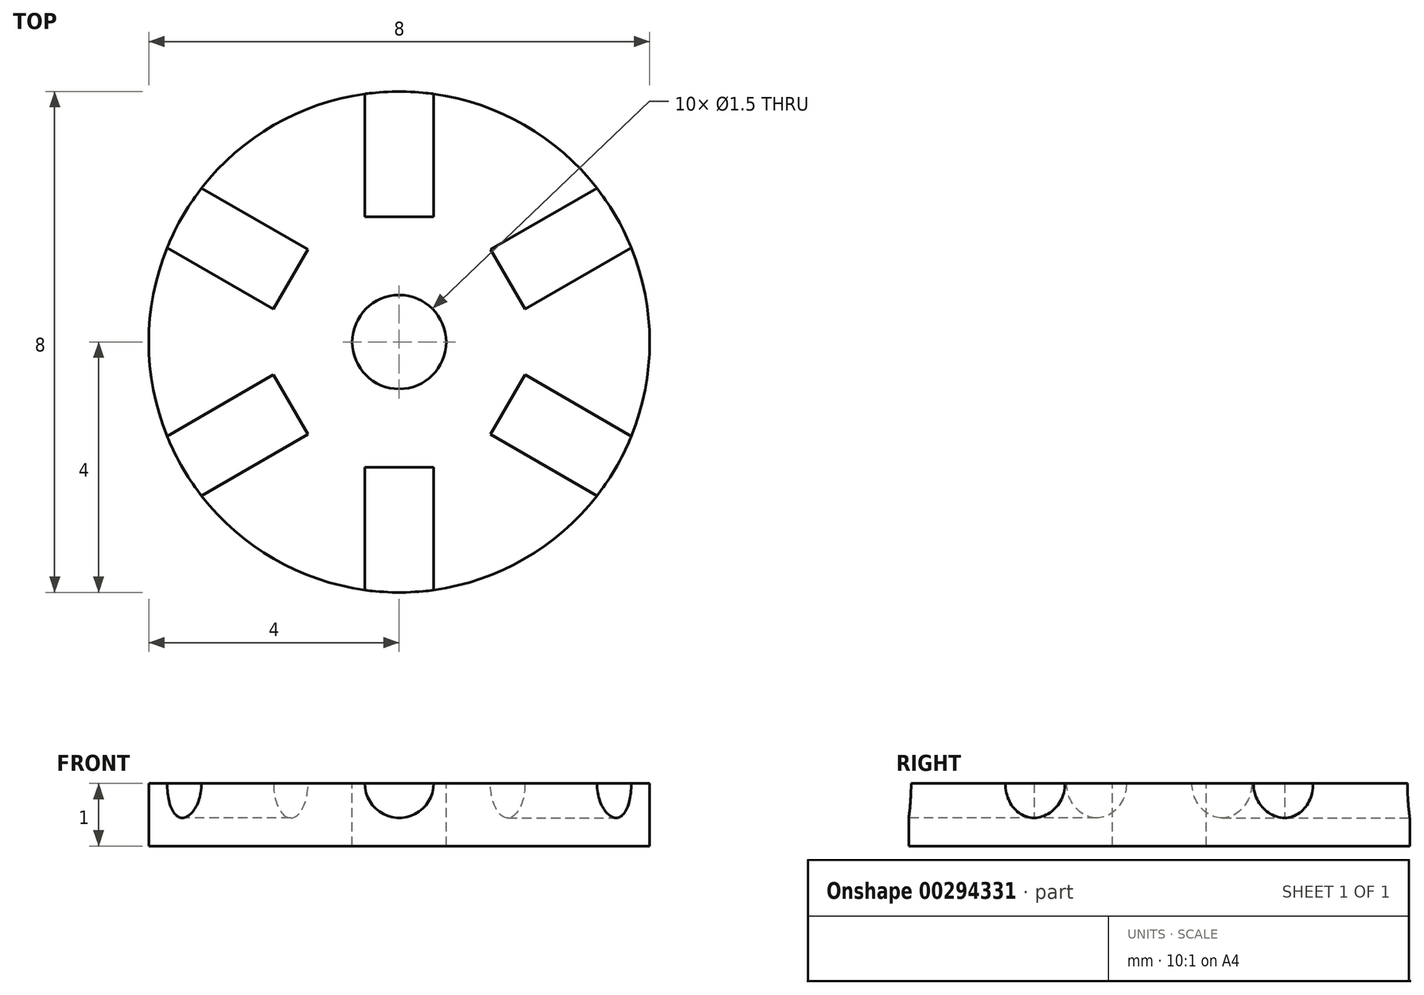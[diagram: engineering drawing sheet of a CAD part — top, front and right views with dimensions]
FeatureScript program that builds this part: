
annotation { "Feature Type Name" : "Feature", "Feature Type Description" : "" }
export const myFeature = defineFeature(function(context is Context, id is Id, definition is map)
    precondition{}
    {
        {
            var Q0;
            Q0=qCreatedBy(makeId("Top.planeOp"),FACE);
            var sketch = newSketch(context, id + "F0", { "sketchPlane" : qUnion([Q0])});
            skCircle(sketch, "E0", {"center": v(0, 0) * mm, "radius": 4 * mm});
            skSolve(sketch);
        }
        {
            var Q0;
            Q0=qSketchRegion(id+"F0",true);
            extrude(context, id + "F1", {"entities" : qUnion([Q0]), "depth" : 1 * mm});
        }
        {
            var Q0;
            Q0=qCreatedBy(makeId("Front.planeOp"),FACE);
            cPlane(context, id + "F2", {"entities" : qUnion([Q0]), "cplaneType" : CPlaneType.OFFSET, "offset" : 4 * mm, "width" : 150 * mm, "height" : 150 * mm});
        }
        {
            var Q0;
            Q0=qCreatedBy(id+"F2.planeOp",FACE);
            var sketch = newSketch(context, id + "F3", { "sketchPlane" : qUnion([Q0])});
            skCircle(sketch, "E1", {"center": v(0, 1) * mm, "radius": 0.55 * mm});
            skSolve(sketch);
        }
        {
            var Q0;
            Q0=makeQuery(id+"F3.imprint","IMPRINT",FACE,{"disambiguationData":[TD([[makeQuery(id+"F3.imprint","IMPRINT",EDGE,{"derivedFrom":sQuery(id+"F3.wireOp",EDGE,"E1")}),1.0]])]});
            extrude(context, id + "F4", {"entities" : qUnion([Q0]), "oppositeDirection" : true, "depth" : 2 * mm});
        }
        {
            var Q0;
            Q0=qCreatedBy(makeId("Right.planeOp"),FACE);
            var sketch = newSketch(context, id + "F5", { "sketchPlane" : qUnion([Q0])});
            skLineSegment(sketch, "E2", {"start": v(0, -9.01) * mm, "end": v(0, 11.79) * mm});
            skSolve(sketch);
        }
        {
            var Q0;
            Q0=makeQuery(id+"F4.opExtrude","SWEPT_BODY",BODY,{"disambiguationData":[OSD([sQuery(id+"F3.wireOp",EDGE,"E1")])]});
            var Q1;
            Q1=sQuery(id+"F5.wireOp",EDGE,"E2");
            circularPattern(context, id + "F6", {"operationType" : NewBodyOperationType.REMOVE, "entities" : qUnion([Q0]), "axis" : qUnion([Q1]), "angle" : 360 * degree, "instanceCount" : 6, "equalSpace" : true});
        }
        {
            var Q0;
            Q0=makeQuery(id+"F1.opExtrude","CAP_FACE",FACE,{"disambiguationData":[OSD([sQuery(id+"F0.wireOp",EDGE,"E0")])],"isStart":false});
            var sketch = newSketch(context, id + "F7", { "sketchPlane" : qUnion([Q0])});
            skCircle(sketch, "E3", {"center": v(0, 0) * mm, "radius": 0.75 * mm});
            skSolve(sketch);
        }
        {
            var Q0;
            Q0=qSketchRegion(id+"F7",true);
            extrude(context, id + "F8", {"entities" : qUnion([Q0]), "operationType" : NewBodyOperationType.REMOVE, "endBound" : BoundingType.UP_TO_NEXT, "oppositeDirection" : true, "depth" : 25 * mm});
        }
    });
